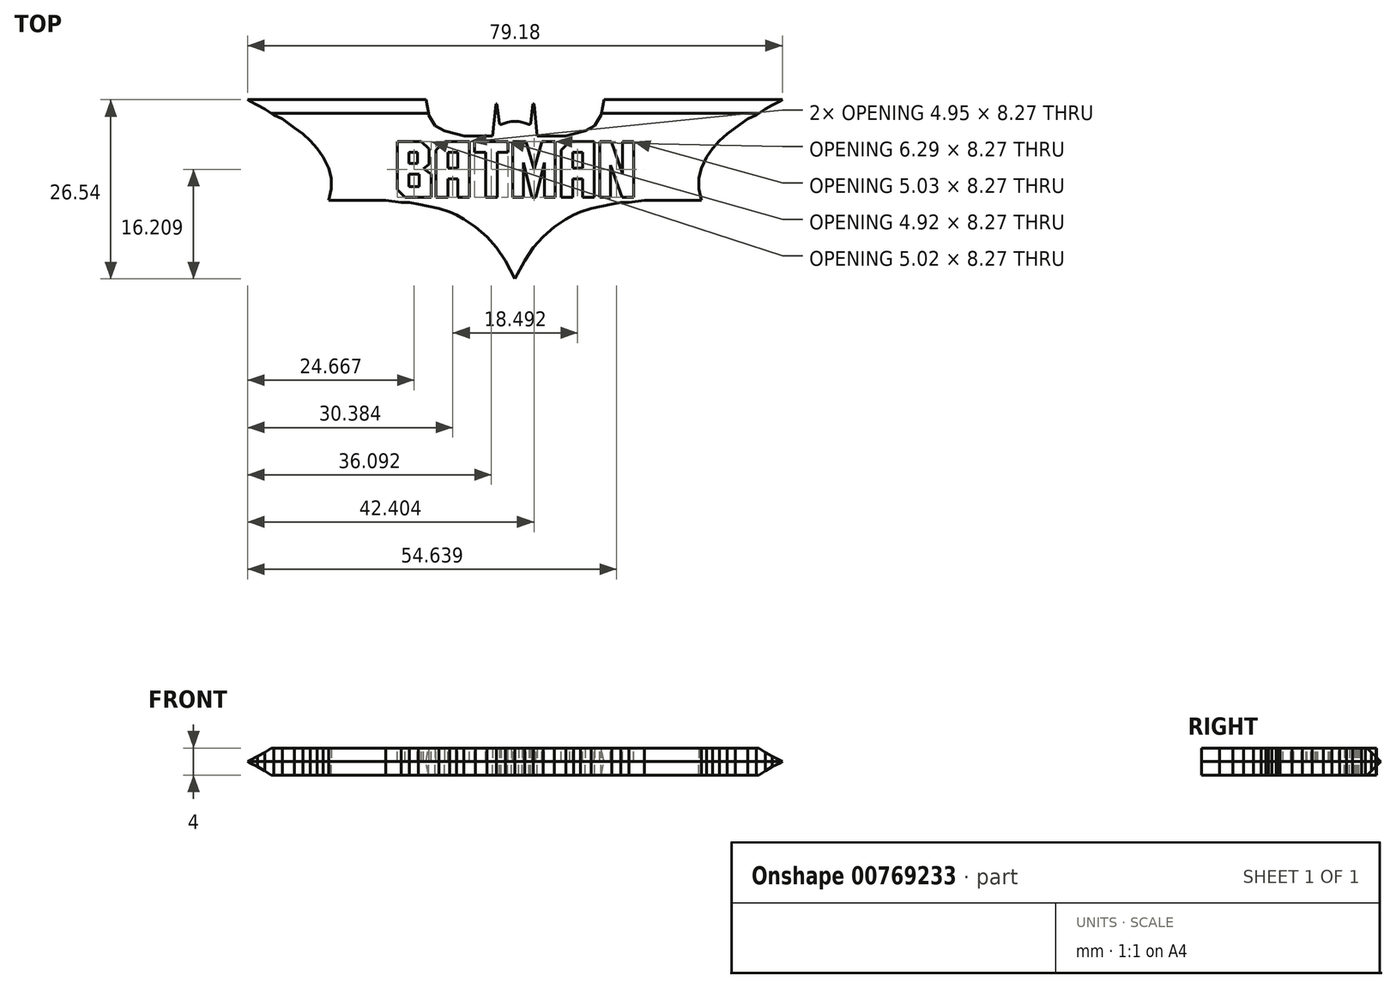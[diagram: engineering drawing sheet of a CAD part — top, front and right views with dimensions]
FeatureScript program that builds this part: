
annotation { "Feature Type Name" : "Feature", "Feature Type Description" : "" }
export const myFeature = defineFeature(function(context is Context, id is Id, definition is map)
    precondition{}
    {
        {
            var Q0;
            Q0=qCreatedBy(makeId("Top.planeOp"),FACE);
            var sketch = newSketch(context, id + "F0", { "sketchPlane" : qUnion([Q0])});
            skLineSegment(sketch, "E0", {"start": v(0, 24.35) * mm, "end": v(-0.54, 24.35) * mm});
            skLineSegment(sketch, "E1", {"start": v(-0.54, 24.35) * mm, "end": v(-1.1, 24.23) * mm});
            skLineSegment(sketch, "E2", {"start": v(-1.1, 24.23) * mm, "end": v(-1.5, 24.08) * mm});
            skLineSegment(sketch, "E3", {"start": v(-1.5, 24.08) * mm, "end": v(-1.88, 23.95) * mm});
            skLineSegment(sketch, "E4", {"start": v(-1.88, 23.95) * mm, "end": v(-2.07, 23.88) * mm});
            skLineSegment(sketch, "E5", {"start": v(-2.07, 23.88) * mm, "end": v(-2.19, 23.88) * mm});
            skLineSegment(sketch, "E6", {"start": v(-2.19, 23.88) * mm, "end": v(-2.25, 23.95) * mm});
            skLineSegment(sketch, "E7", {"start": v(-2.25, 23.95) * mm, "end": v(-2.3, 24.08) * mm});
            skLineSegment(sketch, "E8", {"start": v(-2.3, 24.08) * mm, "end": v(-2.34, 24.35) * mm});
            skLineSegment(sketch, "E9", {"start": v(-2.34, 24.35) * mm, "end": v(-2.4, 24.72) * mm});
            skLineSegment(sketch, "E10", {"start": v(-2.4, 24.72) * mm, "end": v(-2.5, 25.48) * mm});
            skLineSegment(sketch, "E11", {"start": v(-2.5, 25.48) * mm, "end": v(-2.68, 26.96) * mm});
            skLineSegment(sketch, "E12", {"start": v(-2.68, 26.96) * mm, "end": v(-2.76, 26.96) * mm});
            skLineSegment(sketch, "E13", {"start": v(-2.76, 26.96) * mm, "end": v(-2.8, 26.95) * mm});
            skLineSegment(sketch, "E14", {"start": v(-2.8, 26.95) * mm, "end": v(-2.83, 26.88) * mm});
            skLineSegment(sketch, "E15", {"start": v(-2.83, 26.88) * mm, "end": v(-3.29, 22.2) * mm});
            skLineSegment(sketch, "E16", {"start": v(-3.29, 22.2) * mm, "end": v(-6.57, 22.2) * mm});
            skLineSegment(sketch, "E17", {"start": v(-6.57, 22.2) * mm, "end": v(-7.5, 22.2) * mm});
            skLineSegment(sketch, "E18", {"start": v(-7.5, 22.2) * mm, "end": v(-8.7, 22.51) * mm});
            skLineSegment(sketch, "E19", {"start": v(-8.7, 22.51) * mm, "end": v(-10.4, 22.93) * mm});
            skLineSegment(sketch, "E20", {"start": v(-10.4, 22.93) * mm, "end": v(-11.83, 23.73) * mm});
            skLineSegment(sketch, "E21", {"start": v(-11.83, 23.73) * mm, "end": v(-12.76, 25.32) * mm});
            skLineSegment(sketch, "E22", {"start": v(-12.76, 25.32) * mm, "end": v(-13.25, 28.07) * mm});
            skLineSegment(sketch, "E23", {"start": v(-13.25, 28.07) * mm, "end": v(-40.38, 28.07) * mm});
            skLineSegment(sketch, "E24", {"start": v(-40.38, 28.07) * mm, "end": v(-39.34, 27.4) * mm});
            skLineSegment(sketch, "E25", {"start": v(-39.34, 27.4) * mm, "end": v(-38.1, 26.78) * mm});
            skLineSegment(sketch, "E26", {"start": v(-38.1, 26.78) * mm, "end": v(-37.05, 26.2) * mm});
            skLineSegment(sketch, "E27", {"start": v(-37.05, 26.2) * mm, "end": v(-35.73, 25.32) * mm});
            skLineSegment(sketch, "E28", {"start": v(-35.73, 25.32) * mm, "end": v(-34.44, 24.72) * mm});
            skLineSegment(sketch, "E29", {"start": v(-34.44, 24.72) * mm, "end": v(-32.65, 23.38) * mm});
            skLineSegment(sketch, "E30", {"start": v(-32.65, 23.38) * mm, "end": v(-31.4, 22.51) * mm});
            skLineSegment(sketch, "E31", {"start": v(-31.4, 22.51) * mm, "end": v(-30.28, 21.5) * mm});
            skLineSegment(sketch, "E32", {"start": v(-30.28, 21.5) * mm, "end": v(-29.28, 20.34) * mm});
            skLineSegment(sketch, "E33", {"start": v(-29.28, 20.34) * mm, "end": v(-28.37, 19.05) * mm});
            skLineSegment(sketch, "E34", {"start": v(-28.37, 19.05) * mm, "end": v(-27.58, 17.4) * mm});
            skLineSegment(sketch, "E35", {"start": v(-27.58, 17.4) * mm, "end": v(-27.2, 15.98) * mm});
            skLineSegment(sketch, "E36", {"start": v(-27.2, 15.98) * mm, "end": v(-27.2, 14.4) * mm});
            skLineSegment(sketch, "E37", {"start": v(-27.2, 14.4) * mm, "end": v(-27.58, 12.67) * mm});
            skLineSegment(sketch, "E38", {"start": v(-27.58, 12.67) * mm, "end": v(-26.4, 12.67) * mm});
            skLineSegment(sketch, "E39", {"start": v(-26.4, 12.67) * mm, "end": v(-23.8, 12.67) * mm});
            skLineSegment(sketch, "E40", {"start": v(-23.8, 12.67) * mm, "end": v(-22.6, 12.67) * mm});
            skLineSegment(sketch, "E41", {"start": v(-22.6, 12.67) * mm, "end": v(-21.11, 12.67) * mm});
            skLineSegment(sketch, "E42", {"start": v(-21.11, 12.67) * mm, "end": v(-19.15, 12.67) * mm});
            skLineSegment(sketch, "E43", {"start": v(-19.15, 12.67) * mm, "end": v(-16.85, 12.32) * mm});
            skLineSegment(sketch, "E44", {"start": v(-16.85, 12.32) * mm, "end": v(-15.64, 12.32) * mm});
            skLineSegment(sketch, "E45", {"start": v(-15.64, 12.32) * mm, "end": v(-14.31, 12.1) * mm});
            skLineSegment(sketch, "E46", {"start": v(-14.31, 12.1) * mm, "end": v(-11.28, 11.47) * mm});
            skLineSegment(sketch, "E47", {"start": v(-11.28, 11.47) * mm, "end": v(-9.68, 10.94) * mm});
            skLineSegment(sketch, "E48", {"start": v(-9.68, 10.94) * mm, "end": v(-8.66, 10.53) * mm});
            skLineSegment(sketch, "E49", {"start": v(-8.66, 10.53) * mm, "end": v(-7.57, 9.87) * mm});
            skLineSegment(sketch, "E50", {"start": v(-7.57, 9.87) * mm, "end": v(-5.83, 8.72) * mm});
            skLineSegment(sketch, "E51", {"start": v(-5.83, 8.72) * mm, "end": v(-4.15, 7.29) * mm});
            skLineSegment(sketch, "E52", {"start": v(-4.15, 7.29) * mm, "end": v(-2.74, 5.7) * mm});
            skLineSegment(sketch, "E53", {"start": v(-2.74, 5.7) * mm, "end": v(-1.44, 3.7) * mm});
            skLineSegment(sketch, "E54", {"start": v(-1.44, 3.7) * mm, "end": v(0, 1.03) * mm});
            skLineSegment(sketch, "E55", {"start": v(0, 1.03) * mm, "end": v(0, 24.35) * mm});
            skLineSegment(sketch, "E56.MirrorCS", {"start": v(2.76, 26.96) * mm, "end": v(2.8, 26.95) * mm});
            skLineSegment(sketch, "E57.MirrorCS", {"start": v(2.8, 26.95) * mm, "end": v(2.83, 26.88) * mm});
            skLineSegment(sketch, "E58.MirrorCS", {"start": v(2.68, 26.96) * mm, "end": v(2.76, 26.96) * mm});
            skLineSegment(sketch, "E59.MirrorCS", {"start": v(2.07, 23.88) * mm, "end": v(2.19, 23.88) * mm});
            skLineSegment(sketch, "E60.MirrorCS", {"start": v(2.19, 23.88) * mm, "end": v(2.25, 23.95) * mm});
            skLineSegment(sketch, "E61.MirrorCS", {"start": v(2.34, 24.35) * mm, "end": v(2.4, 24.72) * mm});
            skLineSegment(sketch, "E62.MirrorCS", {"start": v(2.3, 24.08) * mm, "end": v(2.34, 24.35) * mm});
            skLineSegment(sketch, "E63.MirrorCS", {"start": v(2.25, 23.95) * mm, "end": v(2.3, 24.08) * mm});
            skLineSegment(sketch, "E64.MirrorCS", {"start": v(1.5, 24.08) * mm, "end": v(1.88, 23.95) * mm});
            skLineSegment(sketch, "E65.MirrorCS", {"start": v(1.88, 23.95) * mm, "end": v(2.07, 23.88) * mm});
            skLineSegment(sketch, "E66.MirrorCS", {"start": v(0, 24.35) * mm, "end": v(0.54, 24.35) * mm});
            skLineSegment(sketch, "E67.MirrorCS", {"start": v(0.54, 24.35) * mm, "end": v(1.1, 24.23) * mm});
            skLineSegment(sketch, "E68.MirrorCS", {"start": v(1.1, 24.23) * mm, "end": v(1.5, 24.08) * mm});
            skLineSegment(sketch, "E69.MirrorCS", {"start": v(32.65, 23.38) * mm, "end": v(31.4, 22.51) * mm});
            skLineSegment(sketch, "E70.MirrorCS", {"start": v(28.37, 19.05) * mm, "end": v(27.58, 17.4) * mm});
            skLineSegment(sketch, "E71.MirrorCS", {"start": v(27.58, 12.67) * mm, "end": v(26.4, 12.67) * mm});
            skLineSegment(sketch, "E72.MirrorCS", {"start": v(37.05, 26.2) * mm, "end": v(35.73, 25.32) * mm});
            skLineSegment(sketch, "E73.MirrorCS", {"start": v(7.57, 9.87) * mm, "end": v(5.83, 8.72) * mm});
            skLineSegment(sketch, "E74.MirrorCS", {"start": v(7.5, 22.2) * mm, "end": v(8.7, 22.51) * mm});
            skLineSegment(sketch, "E75.MirrorCS", {"start": v(11.83, 23.73) * mm, "end": v(12.76, 25.32) * mm});
            skLineSegment(sketch, "E76.MirrorCS", {"start": v(27.2, 14.4) * mm, "end": v(27.58, 12.67) * mm});
            skLineSegment(sketch, "E77.MirrorCS", {"start": v(16.85, 12.32) * mm, "end": v(15.64, 12.32) * mm});
            skLineSegment(sketch, "E78.MirrorCS", {"start": v(39.34, 27.4) * mm, "end": v(38.1, 26.78) * mm});
            skLineSegment(sketch, "E79.MirrorCS", {"start": v(35.73, 25.32) * mm, "end": v(34.44, 24.72) * mm});
            skLineSegment(sketch, "E80.MirrorCS", {"start": v(30.28, 21.5) * mm, "end": v(29.28, 20.34) * mm});
            skLineSegment(sketch, "E81.MirrorCS", {"start": v(11.28, 11.47) * mm, "end": v(9.68, 10.94) * mm});
            skLineSegment(sketch, "E82.MirrorCS", {"start": v(22.6, 12.67) * mm, "end": v(21.11, 12.67) * mm});
            skLineSegment(sketch, "E83.MirrorCS", {"start": v(9.68, 10.94) * mm, "end": v(8.66, 10.53) * mm});
            skLineSegment(sketch, "E84.MirrorCS", {"start": v(31.4, 22.51) * mm, "end": v(30.28, 21.5) * mm});
            skLineSegment(sketch, "E85.MirrorCS", {"start": v(27.58, 17.4) * mm, "end": v(27.2, 15.98) * mm});
            skLineSegment(sketch, "E86.MirrorCS", {"start": v(23.8, 12.67) * mm, "end": v(22.6, 12.67) * mm});
            skLineSegment(sketch, "E87.MirrorCS", {"start": v(8.7, 22.51) * mm, "end": v(10.4, 22.93) * mm});
            skLineSegment(sketch, "E88.MirrorCS", {"start": v(40.38, 28.07) * mm, "end": v(39.34, 27.4) * mm});
            skLineSegment(sketch, "E89.MirrorCS", {"start": v(10.4, 22.93) * mm, "end": v(11.83, 23.73) * mm});
            skLineSegment(sketch, "E90.MirrorCS", {"start": v(27.2, 15.98) * mm, "end": v(27.2, 14.4) * mm});
            skLineSegment(sketch, "E91.MirrorCS", {"start": v(38.1, 26.78) * mm, "end": v(37.05, 26.2) * mm});
            skLineSegment(sketch, "E92.MirrorCS", {"start": v(29.28, 20.34) * mm, "end": v(28.37, 19.05) * mm});
            skLineSegment(sketch, "E93.MirrorCS", {"start": v(2.5, 25.48) * mm, "end": v(2.68, 26.96) * mm});
            skLineSegment(sketch, "E94.MirrorCS", {"start": v(8.66, 10.53) * mm, "end": v(7.57, 9.87) * mm});
            skLineSegment(sketch, "E95.MirrorCS", {"start": v(6.57, 22.2) * mm, "end": v(7.5, 22.2) * mm});
            skLineSegment(sketch, "E96.MirrorCS", {"start": v(2.4, 24.72) * mm, "end": v(2.5, 25.48) * mm});
            skLineSegment(sketch, "E97.MirrorCS", {"start": v(15.64, 12.32) * mm, "end": v(14.31, 12.1) * mm});
            skLineSegment(sketch, "E98.MirrorCS", {"start": v(14.31, 12.1) * mm, "end": v(11.28, 11.47) * mm});
            skLineSegment(sketch, "E99.MirrorCS", {"start": v(1.44, 3.7) * mm, "end": v(0, 1.03) * mm});
            skLineSegment(sketch, "E100.MirrorCS", {"start": v(19.15, 12.67) * mm, "end": v(16.85, 12.32) * mm});
            skLineSegment(sketch, "E101.MirrorCS", {"start": v(12.76, 25.32) * mm, "end": v(13.25, 28.07) * mm});
            skLineSegment(sketch, "E102.MirrorCS", {"start": v(2.83, 26.88) * mm, "end": v(3.29, 22.2) * mm});
            skLineSegment(sketch, "E103.MirrorCS", {"start": v(2.74, 5.7) * mm, "end": v(1.44, 3.7) * mm});
            skLineSegment(sketch, "E104.MirrorCS", {"start": v(3.29, 22.2) * mm, "end": v(6.57, 22.2) * mm});
            skLineSegment(sketch, "E105.MirrorCS", {"start": v(34.44, 24.72) * mm, "end": v(32.65, 23.38) * mm});
            skLineSegment(sketch, "E106.MirrorCS", {"start": v(5.83, 8.72) * mm, "end": v(4.15, 7.29) * mm});
            skLineSegment(sketch, "E107.MirrorCS", {"start": v(13.25, 28.07) * mm, "end": v(40.38, 28.07) * mm});
            skLineSegment(sketch, "E108.MirrorCS", {"start": v(21.11, 12.67) * mm, "end": v(19.15, 12.67) * mm});
            skLineSegment(sketch, "E109.MirrorCS", {"start": v(26.4, 12.67) * mm, "end": v(23.8, 12.67) * mm});
            skLineSegment(sketch, "E110.MirrorCS", {"start": v(4.15, 7.29) * mm, "end": v(2.74, 5.7) * mm});
            skSolve(sketch);
        }
        {
            var Q0;
            Q0 = qSketchRegion(id + "F0", true);
            extrude(context, id + "F1", {"entities" : qUnion([Q0]), "depth" : 2 * mm, "offsetDistance" : 25.4 * mm});
        }
        {
            var Q0;
            Q0=makeQuery(id+"F1.opExtrude","CAP_FACE",FACE,{"disambiguationData":[OSD([sQuery(id+"F0.wireOp",EDGE,"E0"),sQuery(id+"F0.wireOp",EDGE,"E1"),sQuery(id+"F0.wireOp",EDGE,"E2"),sQuery(id+"F0.wireOp",EDGE,"E3"),sQuery(id+"F0.wireOp",EDGE,"E4"),sQuery(id+"F0.wireOp",EDGE,"E5"),sQuery(id+"F0.wireOp",EDGE,"E6"),sQuery(id+"F0.wireOp",EDGE,"E7"),sQuery(id+"F0.wireOp",EDGE,"E8"),sQuery(id+"F0.wireOp",EDGE,"E9"),sQuery(id+"F0.wireOp",EDGE,"E10"),sQuery(id+"F0.wireOp",EDGE,"E11"),sQuery(id+"F0.wireOp",EDGE,"E12"),sQuery(id+"F0.wireOp",EDGE,"E13"),sQuery(id+"F0.wireOp",EDGE,"E14"),sQuery(id+"F0.wireOp",EDGE,"E15"),sQuery(id+"F0.wireOp",EDGE,"E16"),sQuery(id+"F0.wireOp",EDGE,"E17"),sQuery(id+"F0.wireOp",EDGE,"E18"),sQuery(id+"F0.wireOp",EDGE,"E19"),sQuery(id+"F0.wireOp",EDGE,"E20"),sQuery(id+"F0.wireOp",EDGE,"E21"),sQuery(id+"F0.wireOp",EDGE,"E22"),sQuery(id+"F0.wireOp",EDGE,"E23"),sQuery(id+"F0.wireOp",EDGE,"E24"),sQuery(id+"F0.wireOp",EDGE,"E25"),sQuery(id+"F0.wireOp",EDGE,"E26"),sQuery(id+"F0.wireOp",EDGE,"E27"),sQuery(id+"F0.wireOp",EDGE,"E28"),sQuery(id+"F0.wireOp",EDGE,"E29"),sQuery(id+"F0.wireOp",EDGE,"E30"),sQuery(id+"F0.wireOp",EDGE,"E31"),sQuery(id+"F0.wireOp",EDGE,"E32"),sQuery(id+"F0.wireOp",EDGE,"E33"),sQuery(id+"F0.wireOp",EDGE,"E34"),sQuery(id+"F0.wireOp",EDGE,"E35"),sQuery(id+"F0.wireOp",EDGE,"E36"),sQuery(id+"F0.wireOp",EDGE,"E37"),sQuery(id+"F0.wireOp",EDGE,"E38"),sQuery(id+"F0.wireOp",EDGE,"E39"),sQuery(id+"F0.wireOp",EDGE,"E40"),sQuery(id+"F0.wireOp",EDGE,"E41"),sQuery(id+"F0.wireOp",EDGE,"E42"),sQuery(id+"F0.wireOp",EDGE,"E43"),sQuery(id+"F0.wireOp",EDGE,"E44"),sQuery(id+"F0.wireOp",EDGE,"E45"),sQuery(id+"F0.wireOp",EDGE,"E46"),sQuery(id+"F0.wireOp",EDGE,"E47"),sQuery(id+"F0.wireOp",EDGE,"E48"),sQuery(id+"F0.wireOp",EDGE,"E49"),sQuery(id+"F0.wireOp",EDGE,"E50"),sQuery(id+"F0.wireOp",EDGE,"E51"),sQuery(id+"F0.wireOp",EDGE,"E52"),sQuery(id+"F0.wireOp",EDGE,"E53"),sQuery(id+"F0.wireOp",EDGE,"E54"),sQuery(id+"F0.wireOp",EDGE,"E56.MirrorCS"),sQuery(id+"F0.wireOp",EDGE,"E57.MirrorCS"),sQuery(id+"F0.wireOp",EDGE,"E58.MirrorCS"),sQuery(id+"F0.wireOp",EDGE,"E59.MirrorCS"),sQuery(id+"F0.wireOp",EDGE,"E60.MirrorCS"),sQuery(id+"F0.wireOp",EDGE,"E61.MirrorCS"),sQuery(id+"F0.wireOp",EDGE,"E62.MirrorCS"),sQuery(id+"F0.wireOp",EDGE,"E63.MirrorCS"),sQuery(id+"F0.wireOp",EDGE,"E64.MirrorCS"),sQuery(id+"F0.wireOp",EDGE,"E65.MirrorCS"),sQuery(id+"F0.wireOp",EDGE,"E66.MirrorCS"),sQuery(id+"F0.wireOp",EDGE,"E67.MirrorCS"),sQuery(id+"F0.wireOp",EDGE,"E68.MirrorCS"),sQuery(id+"F0.wireOp",EDGE,"E69.MirrorCS"),sQuery(id+"F0.wireOp",EDGE,"E70.MirrorCS"),sQuery(id+"F0.wireOp",EDGE,"E71.MirrorCS"),sQuery(id+"F0.wireOp",EDGE,"E72.MirrorCS"),sQuery(id+"F0.wireOp",EDGE,"E73.MirrorCS"),sQuery(id+"F0.wireOp",EDGE,"E74.MirrorCS"),sQuery(id+"F0.wireOp",EDGE,"E75.MirrorCS"),sQuery(id+"F0.wireOp",EDGE,"E76.MirrorCS"),sQuery(id+"F0.wireOp",EDGE,"E77.MirrorCS"),sQuery(id+"F0.wireOp",EDGE,"E78.MirrorCS"),sQuery(id+"F0.wireOp",EDGE,"E79.MirrorCS"),sQuery(id+"F0.wireOp",EDGE,"E80.MirrorCS"),sQuery(id+"F0.wireOp",EDGE,"E81.MirrorCS"),sQuery(id+"F0.wireOp",EDGE,"E82.MirrorCS"),sQuery(id+"F0.wireOp",EDGE,"E83.MirrorCS"),sQuery(id+"F0.wireOp",EDGE,"E84.MirrorCS"),sQuery(id+"F0.wireOp",EDGE,"E85.MirrorCS"),sQuery(id+"F0.wireOp",EDGE,"E86.MirrorCS"),sQuery(id+"F0.wireOp",EDGE,"E87.MirrorCS"),sQuery(id+"F0.wireOp",EDGE,"E88.MirrorCS"),sQuery(id+"F0.wireOp",EDGE,"E89.MirrorCS"),sQuery(id+"F0.wireOp",EDGE,"E90.MirrorCS"),sQuery(id+"F0.wireOp",EDGE,"E91.MirrorCS"),sQuery(id+"F0.wireOp",EDGE,"E92.MirrorCS"),sQuery(id+"F0.wireOp",EDGE,"E93.MirrorCS"),sQuery(id+"F0.wireOp",EDGE,"E94.MirrorCS"),sQuery(id+"F0.wireOp",EDGE,"E95.MirrorCS"),sQuery(id+"F0.wireOp",EDGE,"E96.MirrorCS"),sQuery(id+"F0.wireOp",EDGE,"E97.MirrorCS"),sQuery(id+"F0.wireOp",EDGE,"E98.MirrorCS"),sQuery(id+"F0.wireOp",EDGE,"E99.MirrorCS"),sQuery(id+"F0.wireOp",EDGE,"E100.MirrorCS"),sQuery(id+"F0.wireOp",EDGE,"E101.MirrorCS"),sQuery(id+"F0.wireOp",EDGE,"E102.MirrorCS"),sQuery(id+"F0.wireOp",EDGE,"E103.MirrorCS"),sQuery(id+"F0.wireOp",EDGE,"E104.MirrorCS"),sQuery(id+"F0.wireOp",EDGE,"E105.MirrorCS"),sQuery(id+"F0.wireOp",EDGE,"E106.MirrorCS"),sQuery(id+"F0.wireOp",EDGE,"E107.MirrorCS"),sQuery(id+"F0.wireOp",EDGE,"E108.MirrorCS"),sQuery(id+"F0.wireOp",EDGE,"E109.MirrorCS"),sQuery(id+"F0.wireOp",EDGE,"E110.MirrorCS")])],"isStart":false});
            var sketch = newSketch(context, id + "F2", { "sketchPlane" : qUnion([Q0])});
            skLineSegment(sketch, "E111", {"start": v(-12.41, 16.55) * mm, "end": v(-12.41, 13.1) * mm});
            skLineSegment(sketch, "E112", {"start": v(-12.41, 13.1) * mm, "end": v(-16.3, 13.1) * mm});
            skLineSegment(sketch, "E113", {"start": v(-16.3, 13.1) * mm, "end": v(-17.43, 14.25) * mm});
            skLineSegment(sketch, "E114", {"start": v(-17.43, 14.25) * mm, "end": v(-17.43, 21.37) * mm});
            skLineSegment(sketch, "E115", {"start": v(-17.43, 21.37) * mm, "end": v(-13.89, 21.37) * mm});
            skLineSegment(sketch, "E116", {"start": v(-13.89, 21.37) * mm, "end": v(-12.72, 20.28) * mm});
            skLineSegment(sketch, "E117", {"start": v(-12.72, 20.28) * mm, "end": v(-12.72, 18) * mm});
            skLineSegment(sketch, "E118", {"start": v(-12.72, 18) * mm, "end": v(-13.53, 17.35) * mm});
            skLineSegment(sketch, "E119", {"start": v(-13.53, 17.35) * mm, "end": v(-12.41, 16.55) * mm});
            skLineSegment(sketch, "E120", {"start": v(-14.15, 14.67) * mm, "end": v(-14.15, 16.55) * mm});
            skLineSegment(sketch, "E121", {"start": v(-14.15, 16.55) * mm, "end": v(-15.7, 16.55) * mm});
            skLineSegment(sketch, "E122", {"start": v(-15.7, 16.55) * mm, "end": v(-15.7, 14.67) * mm});
            skLineSegment(sketch, "E123", {"start": v(-15.7, 14.67) * mm, "end": v(-14.15, 14.67) * mm});
            skLineSegment(sketch, "E124", {"start": v(-14.43, 18.1) * mm, "end": v(-14.43, 19.8) * mm});
            skLineSegment(sketch, "E125", {"start": v(-14.43, 19.8) * mm, "end": v(-15.7, 19.8) * mm});
            skLineSegment(sketch, "E126", {"start": v(-15.7, 19.8) * mm, "end": v(-15.7, 18.1) * mm});
            skLineSegment(sketch, "E127", {"start": v(-15.7, 18.1) * mm, "end": v(-14.43, 18.1) * mm});
            skLineSegment(sketch, "E128", {"start": v(-9.94, 13.1) * mm, "end": v(-11.68, 13.1) * mm});
            skLineSegment(sketch, "E129", {"start": v(-11.68, 13.1) * mm, "end": v(-11.68, 20.07) * mm});
            skLineSegment(sketch, "E130", {"start": v(-11.68, 20.07) * mm, "end": v(-10.35, 21.37) * mm});
            skLineSegment(sketch, "E131", {"start": v(-10.35, 21.37) * mm, "end": v(-6.73, 21.37) * mm});
            skLineSegment(sketch, "E132", {"start": v(-6.73, 21.37) * mm, "end": v(-6.73, 13.1) * mm});
            skLineSegment(sketch, "E133", {"start": v(-6.73, 13.1) * mm, "end": v(-8.47, 13.1) * mm});
            skLineSegment(sketch, "E134", {"start": v(-8.47, 13.1) * mm, "end": v(-8.47, 15.82) * mm});
            skLineSegment(sketch, "E135", {"start": v(-8.47, 15.82) * mm, "end": v(-9.94, 15.82) * mm});
            skLineSegment(sketch, "E136", {"start": v(-9.94, 15.82) * mm, "end": v(-9.94, 13.1) * mm});
            skLineSegment(sketch, "E137", {"start": v(-8.47, 17.4) * mm, "end": v(-8.47, 19.8) * mm});
            skLineSegment(sketch, "E138", {"start": v(-8.47, 19.8) * mm, "end": v(-9.94, 19.8) * mm});
            skLineSegment(sketch, "E139", {"start": v(-9.94, 19.8) * mm, "end": v(-9.94, 17.4) * mm});
            skLineSegment(sketch, "E140", {"start": v(-9.94, 17.4) * mm, "end": v(-8.47, 17.4) * mm});
            skLineSegment(sketch, "E141", {"start": v(-1.04, 19.8) * mm, "end": v(-2.6, 19.8) * mm});
            skLineSegment(sketch, "E142", {"start": v(-2.6, 19.8) * mm, "end": v(-2.6, 13.1) * mm});
            skLineSegment(sketch, "E143", {"start": v(-2.6, 13.1) * mm, "end": v(-4.34, 13.1) * mm});
            skLineSegment(sketch, "E144", {"start": v(-4.34, 13.1) * mm, "end": v(-4.34, 19.8) * mm});
            skLineSegment(sketch, "E145", {"start": v(-4.34, 19.8) * mm, "end": v(-5.96, 19.8) * mm});
            skLineSegment(sketch, "E146", {"start": v(-5.96, 19.8) * mm, "end": v(-5.96, 21.37) * mm});
            skLineSegment(sketch, "E147", {"start": v(-5.96, 21.37) * mm, "end": v(-1.04, 21.37) * mm});
            skLineSegment(sketch, "E148", {"start": v(-1.04, 21.37) * mm, "end": v(-1.04, 19.8) * mm});
            skLineSegment(sketch, "E149", {"start": v(3.96, 21.37) * mm, "end": v(5.96, 21.37) * mm});
            skLineSegment(sketch, "E150", {"start": v(5.96, 21.37) * mm, "end": v(5.96, 13.1) * mm});
            skLineSegment(sketch, "E151", {"start": v(5.96, 13.1) * mm, "end": v(4.36, 13.1) * mm});
            skLineSegment(sketch, "E152", {"start": v(4.36, 13.1) * mm, "end": v(4.36, 18.25) * mm});
            skLineSegment(sketch, "E153", {"start": v(4.36, 18.25) * mm, "end": v(3.07, 13.1) * mm});
            skLineSegment(sketch, "E154", {"start": v(3.07, 13.1) * mm, "end": v(2.56, 13.1) * mm});
            skLineSegment(sketch, "E155", {"start": v(2.56, 13.1) * mm, "end": v(1.27, 18.25) * mm});
            skLineSegment(sketch, "E156", {"start": v(1.27, 18.25) * mm, "end": v(1.27, 13.1) * mm});
            skLineSegment(sketch, "E157", {"start": v(1.27, 13.1) * mm, "end": v(-0.33, 13.1) * mm});
            skLineSegment(sketch, "E158", {"start": v(-0.33, 13.1) * mm, "end": v(-0.33, 21.37) * mm});
            skLineSegment(sketch, "E159", {"start": v(-0.33, 21.37) * mm, "end": v(1.67, 21.37) * mm});
            skLineSegment(sketch, "E160", {"start": v(1.67, 21.37) * mm, "end": v(2.81, 17.26) * mm});
            skLineSegment(sketch, "E161", {"start": v(2.81, 17.26) * mm, "end": v(3.96, 21.37) * mm});
            skLineSegment(sketch, "E162", {"start": v(8.55, 13.1) * mm, "end": v(6.81, 13.1) * mm});
            skLineSegment(sketch, "E163", {"start": v(6.81, 13.1) * mm, "end": v(6.81, 20.07) * mm});
            skLineSegment(sketch, "E164", {"start": v(6.81, 20.07) * mm, "end": v(8.15, 21.37) * mm});
            skLineSegment(sketch, "E165", {"start": v(8.15, 21.37) * mm, "end": v(11.76, 21.37) * mm});
            skLineSegment(sketch, "E166", {"start": v(11.76, 21.37) * mm, "end": v(11.76, 13.1) * mm});
            skLineSegment(sketch, "E167", {"start": v(11.76, 13.1) * mm, "end": v(10.03, 13.1) * mm});
            skLineSegment(sketch, "E168", {"start": v(10.03, 13.1) * mm, "end": v(10.03, 15.82) * mm});
            skLineSegment(sketch, "E169", {"start": v(10.03, 15.82) * mm, "end": v(8.55, 15.82) * mm});
            skLineSegment(sketch, "E170", {"start": v(8.55, 15.82) * mm, "end": v(8.55, 13.1) * mm});
            skLineSegment(sketch, "E171", {"start": v(10.03, 17.4) * mm, "end": v(10.03, 19.8) * mm});
            skLineSegment(sketch, "E172", {"start": v(10.03, 19.8) * mm, "end": v(8.55, 19.8) * mm});
            skLineSegment(sketch, "E173", {"start": v(8.55, 19.8) * mm, "end": v(8.55, 17.4) * mm});
            skLineSegment(sketch, "E174", {"start": v(8.55, 17.4) * mm, "end": v(10.03, 17.4) * mm});
            skLineSegment(sketch, "E175", {"start": v(15.93, 16.63) * mm, "end": v(15.93, 21.37) * mm});
            skLineSegment(sketch, "E176", {"start": v(15.93, 21.37) * mm, "end": v(17.57, 21.37) * mm});
            skLineSegment(sketch, "E177", {"start": v(17.57, 21.37) * mm, "end": v(17.57, 13.1) * mm});
            skLineSegment(sketch, "E178", {"start": v(17.57, 13.1) * mm, "end": v(15.85, 13.1) * mm});
            skLineSegment(sketch, "E179", {"start": v(15.85, 13.1) * mm, "end": v(14.16, 17.85) * mm});
            skLineSegment(sketch, "E180", {"start": v(14.16, 17.85) * mm, "end": v(14.16, 13.1) * mm});
            skLineSegment(sketch, "E181", {"start": v(14.16, 13.1) * mm, "end": v(12.53, 13.1) * mm});
            skLineSegment(sketch, "E182", {"start": v(12.53, 13.1) * mm, "end": v(12.53, 21.37) * mm});
            skLineSegment(sketch, "E183", {"start": v(12.53, 21.37) * mm, "end": v(14.25, 21.37) * mm});
            skLineSegment(sketch, "E184", {"start": v(14.25, 21.37) * mm, "end": v(15.93, 16.63) * mm});
            skSolve(sketch);
        }
        {
            var Q0;
            Q0 = qSketchRegion(id + "F2", true);
            extrude(context, id + "F3", {"entities" : qUnion([Q0]), "operationType" : NewBodyOperationType.REMOVE, "oppositeDirection" : true, "depth" : 3.5 * mm, "offsetDistance" : 25.4 * mm});
        }
        {
            var Q0;
            Q0 = qSketchRegion(id + "F0", true);
            extrude(context, id + "F4", {"entities" : qUnion([Q0]), "oppositeDirection" : true, "depth" : 2 * mm, "offsetDistance" : 25.4 * mm});
        }
        {
            var Q0;
            Q0=makeQuery(id+"F4.opExtrude","CAP_EDGE",EDGE,{"disambiguationData":[OSD([sQuery(id+"F0.wireOp",EDGE,"E107.MirrorCS")])],"isStart":false});
            var Q1;
            Q1=makeQuery(id+"F4.opExtrude","CAP_EDGE",EDGE,{"disambiguationData":[OSD([sQuery(id+"F0.wireOp",EDGE,"E23")])],"isStart":false});
            var Q2;
            Q2=makeQuery(id+"F1.opExtrude","CAP_EDGE",EDGE,{"disambiguationData":[OSD([sQuery(id+"F0.wireOp",EDGE,"E107.MirrorCS")])],"isStart":false});
            var Q3;
            Q3=makeQuery(id+"F1.opExtrude","CAP_EDGE",EDGE,{"disambiguationData":[OSD([sQuery(id+"F0.wireOp",EDGE,"E23")])],"isStart":false});
            chamfer(context, id + "F5", {"entities" : qUnion([Q0, Q1, Q2, Q3]), "width" : 2.5 * mm, "tangentPropagation" : true});
        }
    });
